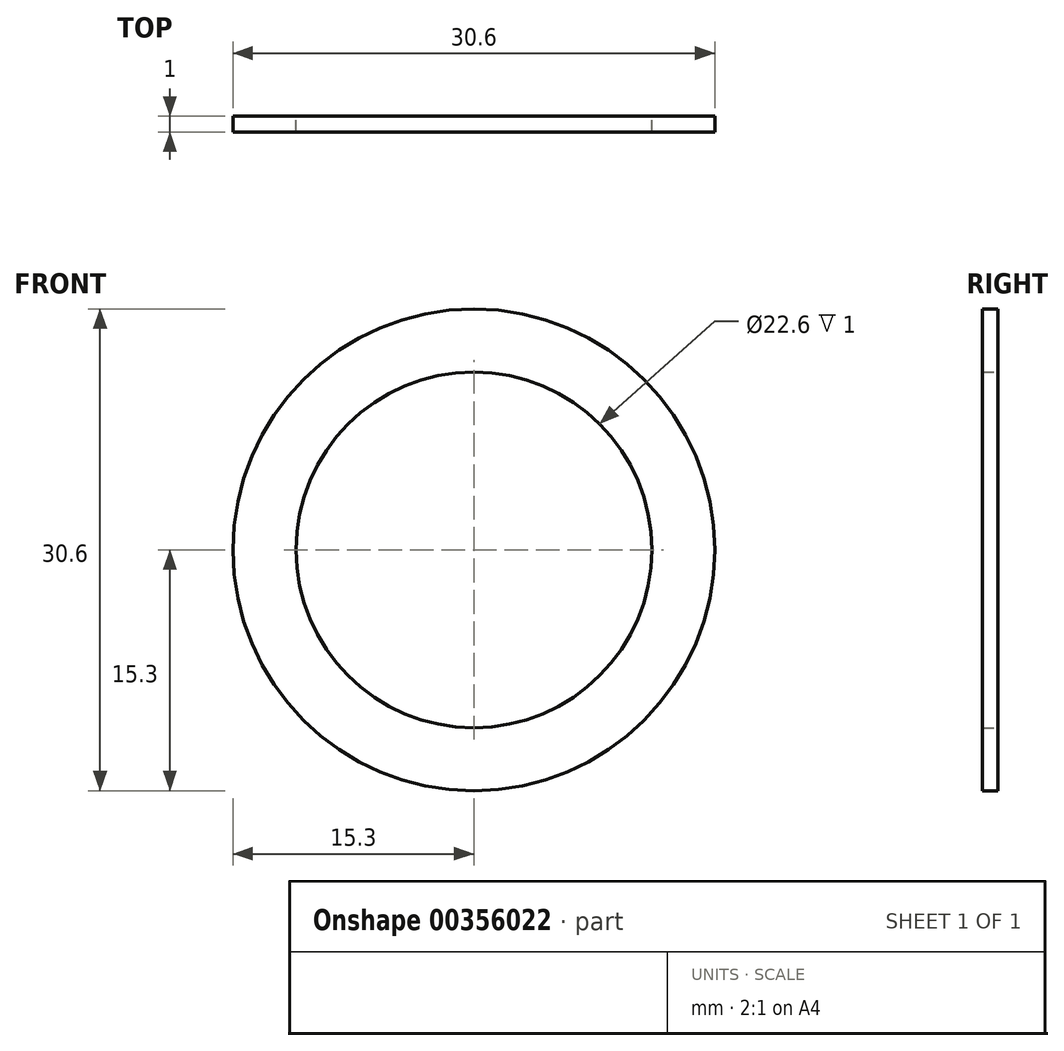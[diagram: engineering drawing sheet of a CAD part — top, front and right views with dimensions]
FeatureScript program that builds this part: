
annotation { "Feature Type Name" : "Feature", "Feature Type Description" : "" }
export const myFeature = defineFeature(function(context is Context, id is Id, definition is map)
    precondition{}
    {
        {
            var Q0;
            Q0=qCreatedBy(makeId("Top.planeOp"),FACE);
            var sketch = newSketch(context, id + "F0", { "sketchPlane" : qUnion([Q0])});
            skLineSegment(sketch, "E0", {"start": v(0, 16.97) * mm, "end": v(0, -12.8) * mm, "construction": true});
            skLineSegment(sketch, "E1.bottom", {"start": v(-11.3, 1.18) * mm, "end": v(-15.3, 1.18) * mm});
            skLineSegment(sketch, "E1.top", {"start": v(-11.3, 2.18) * mm, "end": v(-15.3, 2.18) * mm});
            skLineSegment(sketch, "E1.left", {"start": v(-11.3, 1.18) * mm, "end": v(-11.3, 2.18) * mm});
            skLineSegment(sketch, "E1.right", {"start": v(-15.3, 1.18) * mm, "end": v(-15.3, 2.18) * mm});
            skLineSegment(sketch, "E2.bottom", {"start": v(-15.3, 2.18) * mm, "end": v(-14.3, 2.18) * mm});
            skLineSegment(sketch, "E2.top", {"start": v(-15.3, 5.18) * mm, "end": v(-14.3, 5.18) * mm});
            skLineSegment(sketch, "E2.left", {"start": v(-15.3, 2.18) * mm, "end": v(-15.3, 5.18) * mm});
            skLineSegment(sketch, "E2.right", {"start": v(-14.3, 2.18) * mm, "end": v(-14.3, 5.18) * mm});
            skSolve(sketch);
        }
        {
            var Q0;
            Q0=makeQuery(id+"F0.imprint","IMPRINT",FACE,{"disambiguationData":[TD([[makeQuery(id+"F0.imprint","IMPRINT",EDGE,{"derivedFrom":sQuery(id+"F0.wireOp",EDGE,"E2.bottom")}),1.0]])]});
            var Q1;
            Q1=makeQuery(id+"F0.imprint","IMPRINT",FACE,{"disambiguationData":[TD([[makeQuery(id+"F0.imprint","IMPRINT",EDGE,{"derivedFrom":sQuery(id+"F0.wireOp",EDGE,"E1.bottom")}),-1.0]])]});
            var Q2;
            Q2=sQuery(id+"F0.wireOp",EDGE,"E0");
            revolve(context, id + "F1", {"entities" : qUnion([Q0, Q1]), "axis" : qUnion([Q2]), "revolveType" : RevolveType.FULL});
        }
    });
